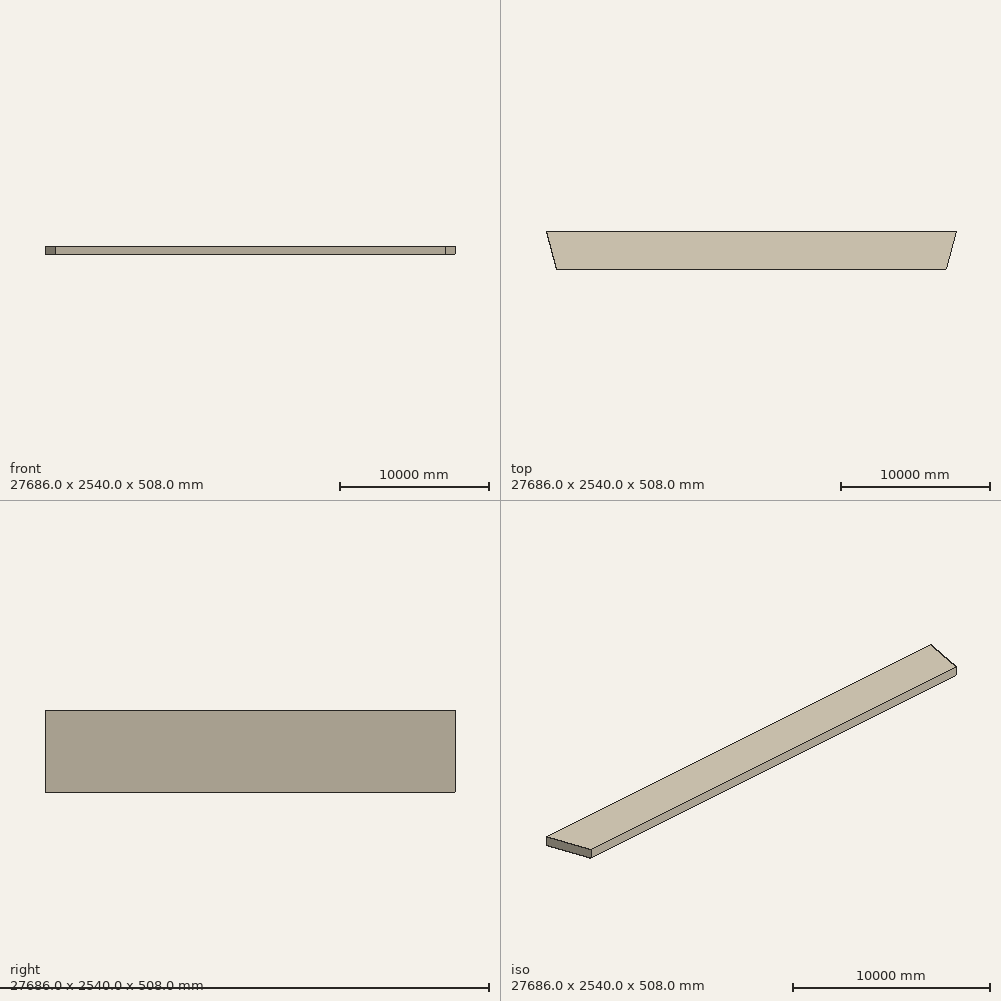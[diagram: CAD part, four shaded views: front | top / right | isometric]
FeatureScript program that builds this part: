
annotation { "Feature Type Name" : "Feature", "Feature Type Description" : "" }
export const myFeature = defineFeature(function(context is Context, id is Id, definition is map)
    precondition{}
    {
        {
            var Q0;
            Q0=qCreatedBy(makeId("Top.planeOp"),FACE);
            var sketch = newSketch(context, id + "F0", { "sketchPlane" : qUnion([Q0])});
            skLineSegment(sketch, "E0", {"start": v(0, 0) * mm, "end": v(27686, 0) * mm});
            skLineSegment(sketch, "E1", {"start": v(27686, 0) * mm, "end": v(27005.4, -2540) * mm});
            skLineSegment(sketch, "E2", {"start": v(27005.4, -2540) * mm, "end": v(680.6, -2540) * mm});
            skLineSegment(sketch, "E3", {"start": v(680.6, -2540) * mm, "end": v(0, 0) * mm});
            skSolve(sketch);
        }
        {
            var Q0;
            Q0 = qSketchRegion(id + "F0", true);
            extrude(context, id + "F1", {"entities" : qUnion([Q0]), "depth" : 508 * mm, "offsetDistance" : 25.4 * mm});
        }
    });
